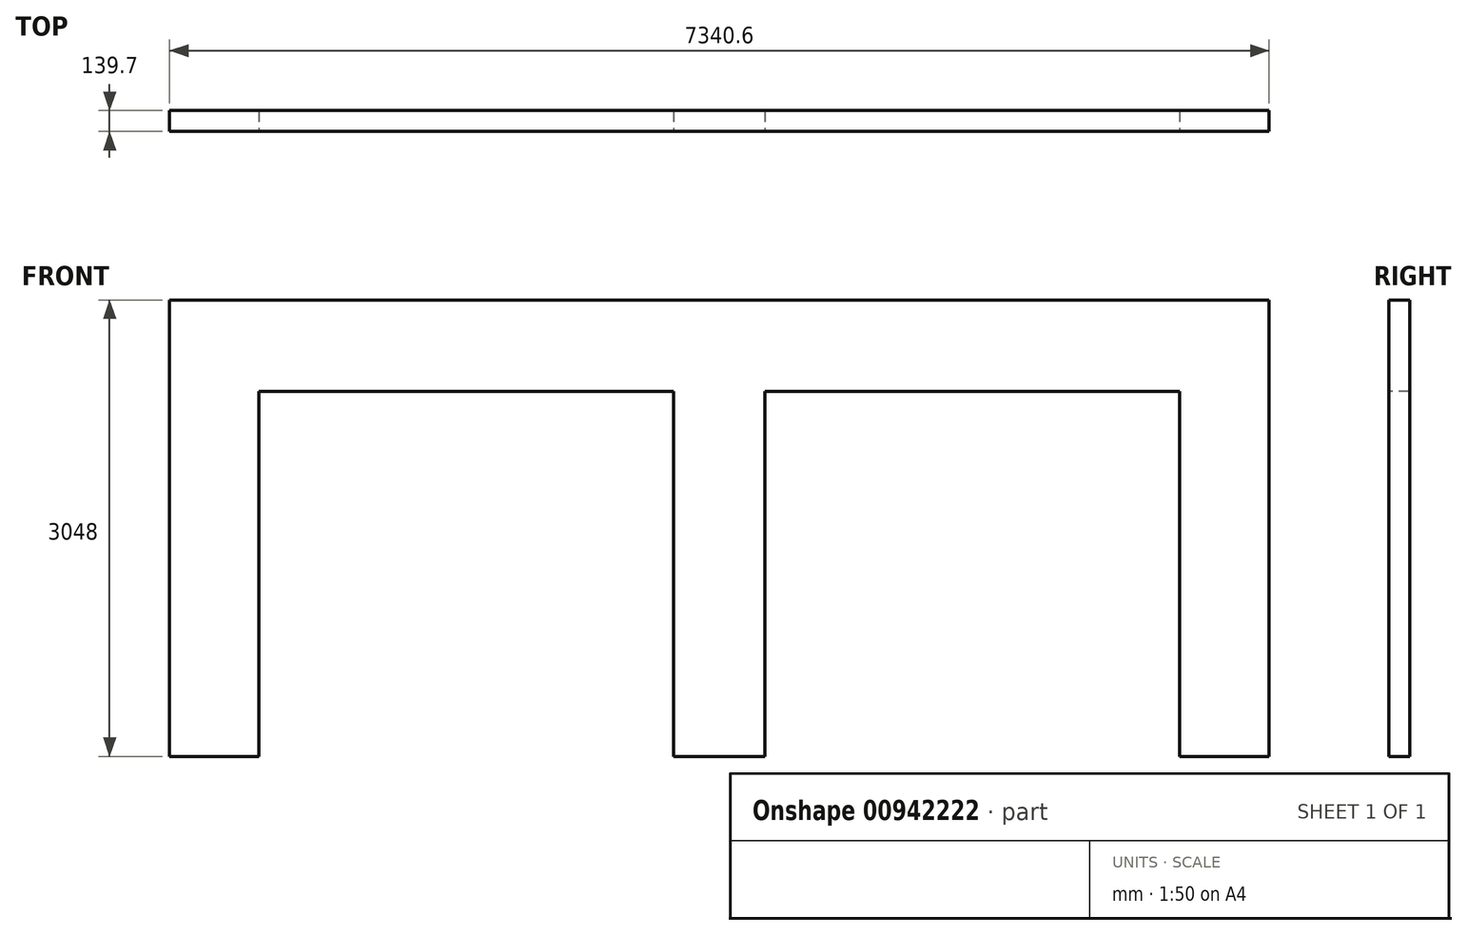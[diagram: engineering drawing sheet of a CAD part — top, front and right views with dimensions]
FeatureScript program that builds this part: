
annotation { "Feature Type Name" : "Feature", "Feature Type Description" : "" }
export const myFeature = defineFeature(function(context is Context, id is Id, definition is map)
    precondition{}
    {
        {
            var Q0;
            Q0=qCreatedBy(makeId("Front.planeOp"),FACE);
            var sketch = newSketch(context, id + "F0", { "sketchPlane" : qUnion([Q0])});
            skLineSegment(sketch, "E0.bottom", {"start": v(0, 0) * mm, "end": v(7340.6, 0) * mm});
            skLineSegment(sketch, "E0.top", {"start": v(0, 3048) * mm, "end": v(7340.6, 3048) * mm});
            skLineSegment(sketch, "E0.left", {"start": v(0, 0) * mm, "end": v(0, 3048) * mm});
            skLineSegment(sketch, "E0.right", {"start": v(7340.6, 0) * mm, "end": v(7340.6, 3048) * mm});
            skSolve(sketch);
        }
        {
            var Q0;
            Q0=makeQuery(id+"F0.imprint","IMPRINT",FACE,{"disambiguationData":[TD([[makeQuery(id+"F0.imprint","IMPRINT",EDGE,{"derivedFrom":sQuery(id+"F0.wireOp",EDGE,"E0.bottom")}),1.0]])]});
            var sketch = newSketch(context, id + "F1", { "sketchPlane" : qUnion([Q0])});
            skLineSegment(sketch, "E1.bottom", {"start": v(596.9, 0) * mm, "end": v(3365.5, 0) * mm});
            skLineSegment(sketch, "E1.top", {"start": v(596.9, 2438.4) * mm, "end": v(3365.5, 2438.4) * mm});
            skLineSegment(sketch, "E1.left", {"start": v(596.9, 0) * mm, "end": v(596.9, 2438.4) * mm});
            skLineSegment(sketch, "E1.right", {"start": v(3365.5, 0) * mm, "end": v(3365.5, 2438.4) * mm});
            skLineSegment(sketch, "E2.bottom", {"start": v(3975.1, 0) * mm, "end": v(6743.7, 0) * mm});
            skLineSegment(sketch, "E2.top", {"start": v(3975.1, 2438.4) * mm, "end": v(6743.7, 2438.4) * mm});
            skLineSegment(sketch, "E2.left", {"start": v(3975.1, 0) * mm, "end": v(3975.1, 2438.4) * mm});
            skLineSegment(sketch, "E2.right", {"start": v(6743.7, 0) * mm, "end": v(6743.7, 2438.4) * mm});
            skPoint(sketch, "E3", {"position": v(3670.3, 0) * mm});
            skSolve(sketch);
        }
        {
            var Q0;
            Q0=makeQuery(id+"F0.imprint","IMPRINT",FACE,{"disambiguationData":[TD([[makeQuery(id+"F0.imprint","IMPRINT",EDGE,{"derivedFrom":sQuery(id+"F0.wireOp",EDGE,"E0.bottom")}),1.0]])]});
            extrude(context, id + "F2", {"entities" : qUnion([Q0]), "oppositeDirection" : true, "depth" : 139.7 * mm, "offsetDistance" : 25.4 * mm});
        }
        {
            var Q0;
            Q0=makeQuery(id+"F1.imprint","IMPRINT",FACE,{"disambiguationData":[TD([[makeQuery(id+"F1.imprint","IMPRINT",EDGE,{"derivedFrom":sQuery(id+"F1.wireOp",EDGE,"E1.bottom")}),1.0]])]});
            var Q1;
            Q1=makeQuery(id+"F1.imprint","IMPRINT",FACE,{"disambiguationData":[TD([[makeQuery(id+"F1.imprint","IMPRINT",EDGE,{"derivedFrom":sQuery(id+"F1.wireOp",EDGE,"E2.bottom")}),1.0]])]});
            extrude(context, id + "F3", {"entities" : qUnion([Q0, Q1]), "operationType" : NewBodyOperationType.REMOVE, "endBound" : BoundingType.THROUGH_ALL, "oppositeDirection" : true, "depth" : 25.4 * mm, "offsetDistance" : 25.4 * mm});
        }
    });
